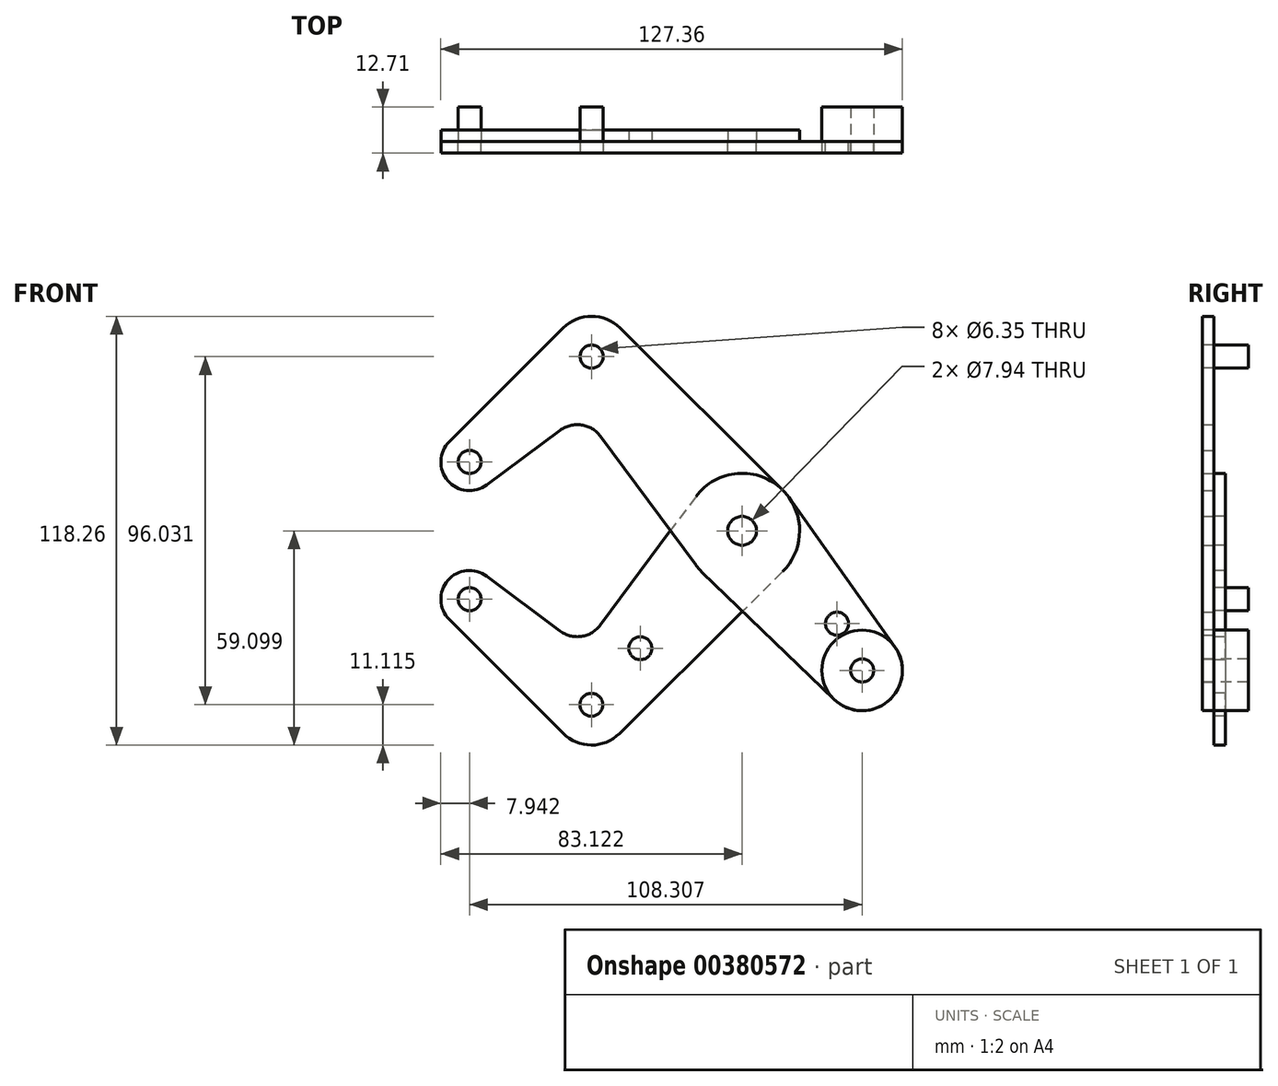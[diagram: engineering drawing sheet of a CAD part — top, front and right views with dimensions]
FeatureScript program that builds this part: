
annotation { "Feature Type Name" : "Feature", "Feature Type Description" : "" }
export const myFeature = defineFeature(function(context is Context, id is Id, definition is map)
    precondition{}
    {
        {
            var Q0;
            Q0=qCreatedBy(makeId("Front.planeOp"),FACE);
            var sketch = newSketch(context, id + "F0", { "sketchPlane" : qUnion([Q0])});
            skLineSegment(sketch, "E0", {"start": v(-14.03, 53.36) * mm, "end": v(66.98, -40.58) * mm, "construction": true});
            skCircle(sketch, "E1", {"center": v(27.5, 5.3) * mm, "radius": 3.18 * mm});
            skCircle(sketch, "E2", {"center": v(60.62, -33.2) * mm, "radius": 3.18 * mm});
            skCircle(sketch, "E3", {"center": v(-14.03, 53.36) * mm, "radius": 3.18 * mm});
            skCircle(sketch, "E4", {"center": v(-47.69, 24.33) * mm, "radius": 3.18 * mm});
            skLineSegment(sketch, "E5", {"start": v(-14.03, 53.36) * mm, "end": v(-47.69, 24.33) * mm, "construction": true});
            skCircle(sketch, "E6", {"center": v(60.62, -33.2) * mm, "radius": 11.11 * mm});
            skCircle(sketch, "E7", {"center": v(-47.69, 24.33) * mm, "radius": 7.94 * mm});
            skCircle(sketch, "E8", {"center": v(-14.03, 53.36) * mm, "radius": 11.11 * mm});
            skLineSegment(sketch, "E9", {"start": v(-53.29, 29.95) * mm, "end": v(-21.87, 61.23) * mm});
            skLineSegment(sketch, "E10", {"start": v(-42.95, 17.96) * mm, "end": v(-22.7, 33.04) * mm});
            skCircle(sketch, "E11", {"center": v(27.5, 5.3) * mm, "radius": 15.88 * mm});
            skLineSegment(sketch, "E12", {"start": v(-6.19, 61.23) * mm, "end": v(38.7, 16.56) * mm});
            skLineSegment(sketch, "E13", {"start": v(-11.59, 31.4) * mm, "end": v(14.74, -4.14) * mm});
            skLineSegment(sketch, "E14", {"start": v(16.48, -6.13) * mm, "end": v(52.91, -41.2) * mm});
            skLineSegment(sketch, "E15", {"start": v(40.44, 14.49) * mm, "end": v(69.69, -26.78) * mm});
            skArc(sketch, "E16.filletArc", {"start": v(-11.59, 31.4) * mm, "mid": v(-16.8, 34.52) * mm, "end": v(-22.7, 33.04) * mm});
            skLineSegment(sketch, "E17", {"start": v(27.5, 5.3) * mm, "end": v(-14.1, -42.67) * mm, "construction": true});
            skLineSegment(sketch, "E18", {"start": v(-14.1, -42.67) * mm, "end": v(-47.69, -13.56) * mm, "construction": true});
            skCircle(sketch, "E19", {"center": v(-47.69, -13.56) * mm, "radius": 3.18 * mm});
            skCircle(sketch, "E20", {"center": v(-14.1, -42.67) * mm, "radius": 3.18 * mm});
            skCircle(sketch, "E21", {"center": v(-47.69, -13.56) * mm, "radius": 7.94 * mm});
            skCircle(sketch, "E22", {"center": v(-14.1, -42.67) * mm, "radius": 11.11 * mm});
            skLineSegment(sketch, "E23", {"start": v(-42.93, -7.2) * mm, "end": v(-22.74, -22.32) * mm});
            skLineSegment(sketch, "E24", {"start": v(-53.3, -19.17) * mm, "end": v(-21.96, -50.53) * mm});
            skLineSegment(sketch, "E25", {"start": v(14.75, 14.78) * mm, "end": v(-11.62, -20.7) * mm});
            skLineSegment(sketch, "E26", {"start": v(38.67, -5.96) * mm, "end": v(-6.27, -50.56) * mm});
            skArc(sketch, "E27.filletArc", {"start": v(-22.74, -22.32) * mm, "mid": v(-16.84, -23.82) * mm, "end": v(-11.62, -20.7) * mm});
            skCircle(sketch, "E28", {"center": v(-0.58, -27.08) * mm, "radius": 3.18 * mm});
            skCircle(sketch, "E29", {"center": v(53.7, -20.31) * mm, "radius": 3.18 * mm});
            skLineSegment(sketch, "E30", {"start": v(53.7, -20.31) * mm, "end": v(51.29, -22.38) * mm, "construction": true});
            skCircle(sketch, "E31", {"center": v(27.5, 5.3) * mm, "radius": 3.97 * mm});
            skSolve(sketch);
        }
        {
            var Q0;
            {var subQ6=sQuery(id+"F0.wireOp",EDGE,"E9");Q0=makeQuery(id+"F0.imprint","IMPRINT",FACE,{"disambiguationData":[TD([[makeQuery(id+"F0.imprint","IMPRINT",EDGE,{"derivedFrom":subQ6}),-1.0]])]});}
            var Q1;
            {var subQ0=sQuery(id+"F0.wireOp",EDGE,"E15");Q1=makeQuery(id+"F0.imprint","IMPRINT",FACE,{"disambiguationData":[TD([[makeQuery(id+"F0.imprint","IMPRINT",EDGE,{"derivedFrom":subQ0}),-1.0]])]});}
            var Q2;
            Q2=makeQuery(id+"F0.imprint","IMPRINT",FACE,{"disambiguationData":[TD([[makeQuery(id+"F0.imprint","IMPRINT",EDGE,{"derivedFrom":sQuery(id+"F0.wireOp",EDGE,"E3")}),-1.0]])]});
            var Q3;
            Q3=makeQuery(id+"F0.imprint","IMPRINT",FACE,{"disambiguationData":[TD([[makeQuery(id+"F0.imprint","IMPRINT",EDGE,{"derivedFrom":sQuery(id+"F0.wireOp",EDGE,"E4")}),-1.0]])]});
            var Q4;
            Q4=makeQuery(id+"F0.imprint","IMPRINT",FACE,{"disambiguationData":[TD([[makeQuery(id+"F0.imprint","IMPRINT",EDGE,{"derivedFrom":sQuery(id+"F0.wireOp",EDGE,"E2")}),-1.0]])]});
            var Q5;
            Q5=makeQuery(id+"F0.imprint","IMPRINT",FACE,{"disambiguationData":[TD([[makeQuery(id+"F0.imprint","IMPRINT",EDGE,{"derivedFrom":sQuery(id+"F0.wireOp",EDGE,"E31")}),-1.0]])]});
            var Q6;
            {var subQ0=sQuery(id+"F0.wireOp",EDGE,"E13");var subQ1=sQuery(id+"F0.wireOp",EDGE,"E11");var subQ2=makeQuery(id+"F0.imprint","INTERSECT",VERTEX,{"derivedFrom":[subQ1,subQ0]});Q6=makeQuery(id+"F0.imprint","IMPRINT",FACE,{"disambiguationData":[TD([[makeQuery(id+"F0.imprint","IMPRINT",EDGE,{"disambiguationData":[TD([[subQ2,1.0]])],"derivedFrom":subQ1}),-1.0]])]});}
            var Q7;
            {var subQ0=sQuery(id+"F0.wireOp",EDGE,"E14");var subQ1=sQuery(id+"F0.wireOp",EDGE,"E11");var subQ2=makeQuery(id+"F0.imprint","INTERSECT",VERTEX,{"derivedFrom":[subQ1,subQ0]});Q7=makeQuery(id+"F0.imprint","IMPRINT",FACE,{"disambiguationData":[TD([[makeQuery(id+"F0.imprint","IMPRINT",EDGE,{"disambiguationData":[TD([[subQ2,-1.0]])],"derivedFrom":subQ1}),-1.0]])]});}
            extrude(context, id + "F1", {"entities" : qUnion([Q0, Q1, Q2, Q3, Q4, Q5, Q6, Q7]), "depth" : 3.17 * mm});
        }
        {
            var Q0;
            Q0=makeQuery(id+"F0.imprint","IMPRINT",FACE,{"disambiguationData":[TD([[makeQuery(id+"F0.imprint","IMPRINT",EDGE,{"derivedFrom":sQuery(id+"F0.wireOp",EDGE,"E20")}),-1.0]])]});
            var Q1;
            Q1=makeQuery(id+"F0.imprint","IMPRINT",FACE,{"disambiguationData":[TD([[makeQuery(id+"F0.imprint","IMPRINT",EDGE,{"derivedFrom":sQuery(id+"F0.wireOp",EDGE,"E19")}),-1.0]])]});
            var Q2;
            {var subQ0=sQuery(id+"F0.wireOp",EDGE,"E14");var subQ1=sQuery(id+"F0.wireOp",EDGE,"E11");var subQ2=makeQuery(id+"F0.imprint","INTERSECT",VERTEX,{"derivedFrom":[subQ1,subQ0]});Q2=makeQuery(id+"F0.imprint","IMPRINT",FACE,{"disambiguationData":[TD([[makeQuery(id+"F0.imprint","IMPRINT",EDGE,{"disambiguationData":[TD([[subQ2,-1.0]])],"derivedFrom":subQ1}),-1.0]])]});}
            var Q3;
            Q3=makeQuery(id+"F0.imprint","IMPRINT",FACE,{"disambiguationData":[TD([[makeQuery(id+"F0.imprint","IMPRINT",EDGE,{"derivedFrom":sQuery(id+"F0.wireOp",EDGE,"E31")}),-1.0]])]});
            var Q4;
            {var subQ13=sQuery(id+"F0.wireOp",EDGE,"E23");Q4=makeQuery(id+"F0.imprint","IMPRINT",FACE,{"disambiguationData":[TD([[makeQuery(id+"F0.imprint","IMPRINT",EDGE,{"derivedFrom":subQ13}),-1.0]])]});}
            var Q5;
            {var subQ0=sQuery(id+"F0.wireOp",EDGE,"E13");var subQ1=sQuery(id+"F0.wireOp",EDGE,"E11");var subQ2=makeQuery(id+"F0.imprint","INTERSECT",VERTEX,{"derivedFrom":[subQ1,subQ0]});Q5=makeQuery(id+"F0.imprint","IMPRINT",FACE,{"disambiguationData":[TD([[makeQuery(id+"F0.imprint","IMPRINT",EDGE,{"disambiguationData":[TD([[subQ2,1.0]])],"derivedFrom":subQ1}),-1.0]])]});}
            extrude(context, id + "F2", {"entities" : qUnion([Q0, Q1, Q2, Q3, Q4, Q5]), "oppositeDirection" : true, "depth" : 3.17 * mm});
        }
        {
            var Q0;
            Q0=makeQuery(id+"F1.opExtrude","CAP_FACE",FACE,{"disambiguationData":[OSD([sQuery(id+"F0.wireOp",EDGE,"E2"),sQuery(id+"F0.wireOp",EDGE,"E3"),sQuery(id+"F0.wireOp",EDGE,"E4"),sQuery(id+"F0.wireOp",EDGE,"E6"),sQuery(id+"F0.wireOp",EDGE,"E7"),sQuery(id+"F0.wireOp",EDGE,"E8"),sQuery(id+"F0.wireOp",EDGE,"E9"),sQuery(id+"F0.wireOp",EDGE,"E10"),sQuery(id+"F0.wireOp",EDGE,"E11"),sQuery(id+"F0.wireOp",EDGE,"E12"),sQuery(id+"F0.wireOp",EDGE,"E13"),sQuery(id+"F0.wireOp",EDGE,"E14"),sQuery(id+"F0.wireOp",EDGE,"E15"),sQuery(id+"F0.wireOp",EDGE,"E16.filletArc"),sQuery(id+"F0.wireOp",EDGE,"E29"),sQuery(id+"F0.wireOp",EDGE,"E31")])],"isStart":false});
            var sketch = newSketch(context, id + "F3", { "sketchPlane" : qUnion([Q0])});
            skCircle(sketch, "E32", {"center": v(-14.03, 53.36) * mm, "radius": 3.98 * mm});
            skCircle(sketch, "E33", {"center": v(27.5, 5.3) * mm, "radius": 3.98 * mm});
            skCircle(sketch, "E34", {"center": v(60.62, -33.2) * mm, "radius": 11.11 * mm});
            skSolve(sketch);
        }
        {
            var Q0;
            Q0=makeQuery(id+"F2.opExtrude","CAP_FACE",FACE,{"disambiguationData":[OSD([sQuery(id+"F0.wireOp",EDGE,"E11"),sQuery(id+"F0.wireOp",EDGE,"E13"),sQuery(id+"F0.wireOp",EDGE,"E14"),sQuery(id+"F0.wireOp",EDGE,"E19"),sQuery(id+"F0.wireOp",EDGE,"E20"),sQuery(id+"F0.wireOp",EDGE,"E21"),sQuery(id+"F0.wireOp",EDGE,"E22"),sQuery(id+"F0.wireOp",EDGE,"E23"),sQuery(id+"F0.wireOp",EDGE,"E24"),sQuery(id+"F0.wireOp",EDGE,"E25"),sQuery(id+"F0.wireOp",EDGE,"E26"),sQuery(id+"F0.wireOp",EDGE,"E27.filletArc"),sQuery(id+"F0.wireOp",EDGE,"E28")])],"isStart":true});
            var sketch = newSketch(context, id + "F4", { "sketchPlane" : qUnion([Q0])});
            skCircle(sketch, "E35", {"center": v(-14.1, -42.67) * mm, "radius": 11.11 * mm});
            skLineSegment(sketch, "E36", {"start": v(-14.1, -42.67) * mm, "end": v(-7.8, -41.88) * mm});
            skLineSegment(sketch, "E37", {"start": v(-7.8, -41.88) * mm, "end": v(-8.95, -32.83) * mm});
            skLineSegment(sketch, "E38", {"start": v(-8.95, -32.83) * mm, "end": v(-7.8, -41.88) * mm});
            skLineSegment(sketch, "E39", {"start": v(-7.8, -41.88) * mm, "end": v(-6.65, -50.92) * mm});
            skSolve(sketch);
        }
        {
            var Q0;
            Q0=qCreatedBy(makeId("Front.planeOp"),FACE);
            cPlane(context, id + "F5", {"entities" : qUnion([Q0]), "cplaneType" : CPlaneType.OFFSET, "offset" : 9.52 * mm, "oppositeDirection" : true, "width" : 152.4 * mm, "height" : 152.4 * mm});
        }
        {
            var Q0;
            Q0=makeQuery(id+"F4.imprint","IMPRINT",FACE,{"disambiguationData":[TD([[makeQuery(id+"F4.imprint","IMPRINT",EDGE,{"derivedFrom":makeQuery(id+"F2.opExtrude","CAP_EDGE",EDGE,{"disambiguationData":[OSD([sQuery(id+"F0.wireOp",EDGE,"E19")])],"isStart":true})}),1.0]])]});
            var Q1;
            Q1=makeQuery(id+"F3.imprint","IMPRINT",FACE,{"disambiguationData":[TD([[makeQuery(id+"F3.imprint","IMPRINT",EDGE,{"derivedFrom":makeQuery(id+"F1.opExtrude","CAP_EDGE",EDGE,{"disambiguationData":[OSD([sQuery(id+"F0.wireOp",EDGE,"E2")])],"isStart":false})}),-1.0]])]});
            var Q2;
            {var subQ0=sQuery(id+"F4.wireOp",EDGE,"E38");Q2=makeQuery(id+"F4.imprint","IMPRINT",FACE,{"disambiguationData":[TD([[makeQuery(id+"F4.imprint","IMPRINT",EDGE,{"derivedFrom":subQ0}),-1.0]])]});}
            var Q3;
            Q3=makeQuery(id+"F3.imprint","IMPRINT",FACE,{"disambiguationData":[TD([[makeQuery(id+"F3.imprint","IMPRINT",EDGE,{"derivedFrom":makeQuery(id+"F1.opExtrude","CAP_EDGE",EDGE,{"disambiguationData":[OSD([sQuery(id+"F0.wireOp",EDGE,"E3")])],"isStart":false})}),1.0]])]});
            var Q4;
            Q4=qCreatedBy(id+"F5.planeOp",FACE);
            extrude(context, id + "F6", {"entities" : qUnion([Q0, Q1, Q2, Q3]), "endBound" : BoundingType.UP_TO_SURFACE, "oppositeDirection" : true, "endBoundEntityFace" : qUnion([Q4]), "depth" : 25.4 * mm});
        }
    });
